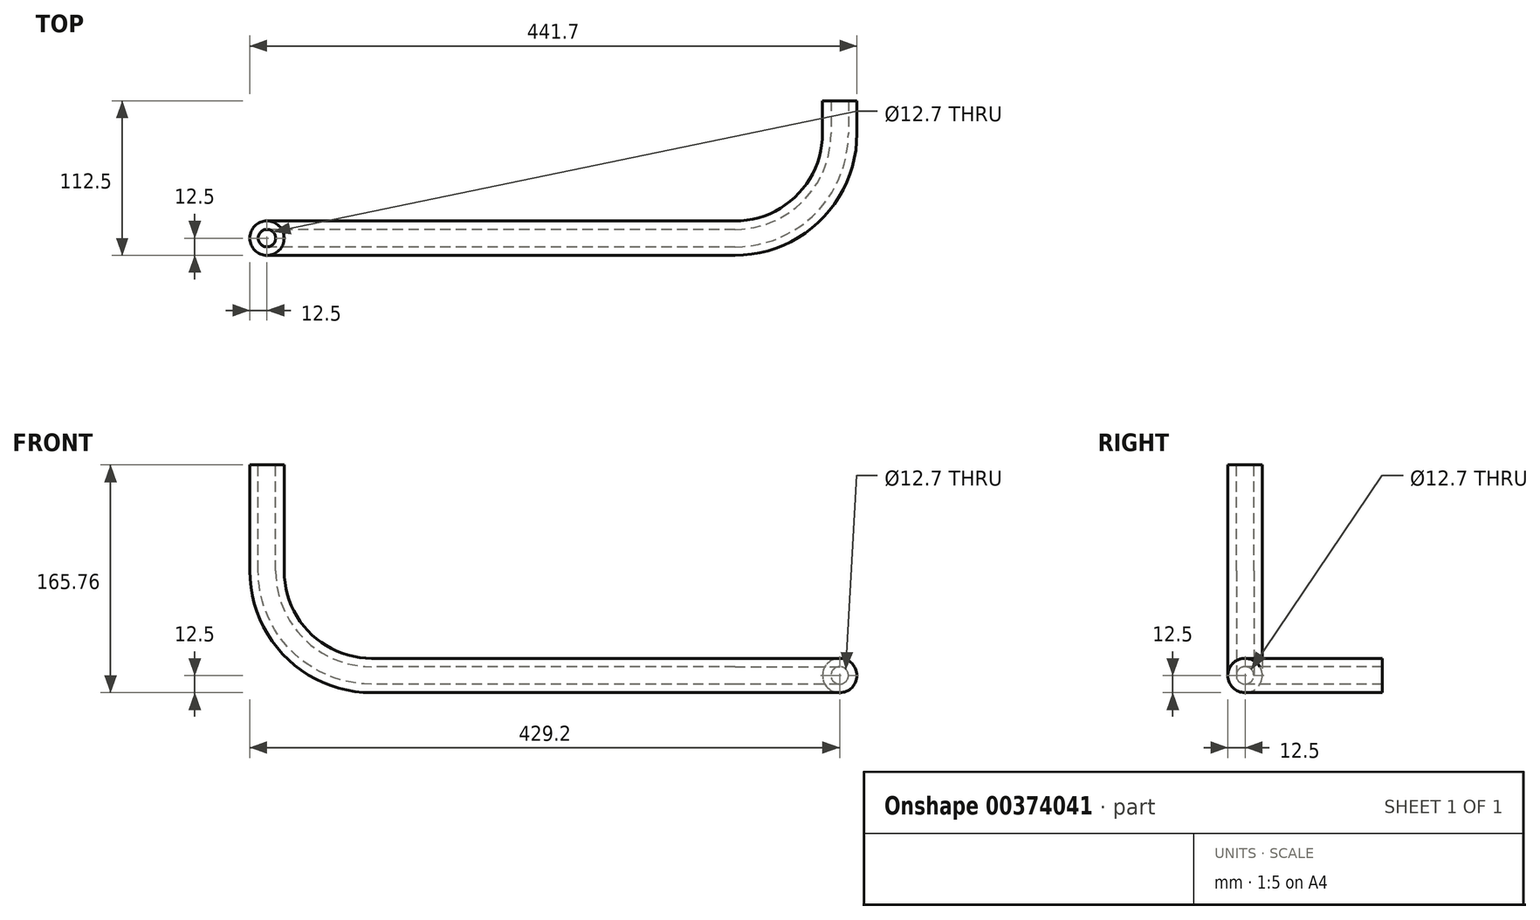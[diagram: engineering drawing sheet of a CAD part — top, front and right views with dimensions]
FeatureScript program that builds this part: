
annotation { "Feature Type Name" : "Feature", "Feature Type Description" : "" }
export const myFeature = defineFeature(function(context is Context, id is Id, definition is map)
    precondition{}
    {
        {
            var Q0;
            Q0=qCreatedBy(makeId("Front.planeOp"),FACE);
            var sketch = newSketch(context, id + "F0", { "sketchPlane" : qUnion([Q0])});
            skCircle(sketch, "E0", {"center": v(0, 0) * mm, "radius": 6.35 * mm});
            skCircle(sketch, "E1", {"center": v(0, 0) * mm, "radius": 12.5 * mm});
            skSolve(sketch);
        }
        {
            var Q0;
            Q0=qCreatedBy(makeId("Top.planeOp"),FACE);
            var sketch = newSketch(context, id + "F1", { "sketchPlane" : qUnion([Q0])});
            skLineSegment(sketch, "E2", {"start": v(0, 0) * mm, "end": v(0, -23.8) * mm});
            skLineSegment(sketch, "E3", {"start": v(-76.2, -100) * mm, "end": v(-340.5, -100) * mm});
            skPoint(sketch, "E4.visualSharp", {"position": v(0, -100) * mm});
            skArc(sketch, "E4.filletArc", {"start": v(-76.2, -100) * mm, "mid": v(-22.32, -77.68) * mm, "end": v(0, -23.8) * mm});
            skSolve(sketch);
        }
        {
            var Q0;
            Q0=qCreatedBy(makeId("Front.planeOp"),FACE);
            cPlane(context, id + "F2", {"entities" : qUnion([Q0]), "cplaneType" : CPlaneType.OFFSET, "offset" : 100 * mm, "width" : 150 * mm, "height" : 150 * mm});
        }
        {
            var Q0;
            Q0=qCreatedBy(id+"F2.planeOp",FACE);
            var sketch = newSketch(context, id + "F3", { "sketchPlane" : qUnion([Q0])});
            skLineSegment(sketch, "E5", {"start": v(-340.5, 0) * mm, "end": v(-340.5, 76.2) * mm, "construction": true});
            skArc(sketch, "E6", {"start": v(-340.5, 0) * mm, "mid": v(-394.38, 22.32) * mm, "end": v(-416.7, 76.2) * mm});
            skLineSegment(sketch, "E7", {"start": v(-416.7, 76.2) * mm, "end": v(-416.7, 153.26) * mm});
            skSolve(sketch);
        }
        {
            var Q0;
            Q0 = qSketchRegion(id + "F0", true);
            var Q1;
            Q1 = qConstructionFilter(qBodyType(qCreatedBy(id + "F1" ,EDGE), BodyType.WIRE), ConstructionObject.NO);
            var Q2;
            Q2 = qConstructionFilter(qBodyType(qCreatedBy(id + "F3" ,EDGE), BodyType.WIRE), ConstructionObject.NO);
            sweep(context, id + "F4", {"profiles" : qUnion([Q0]), "path" : qUnion([Q1, Q2])});
        }
    });
